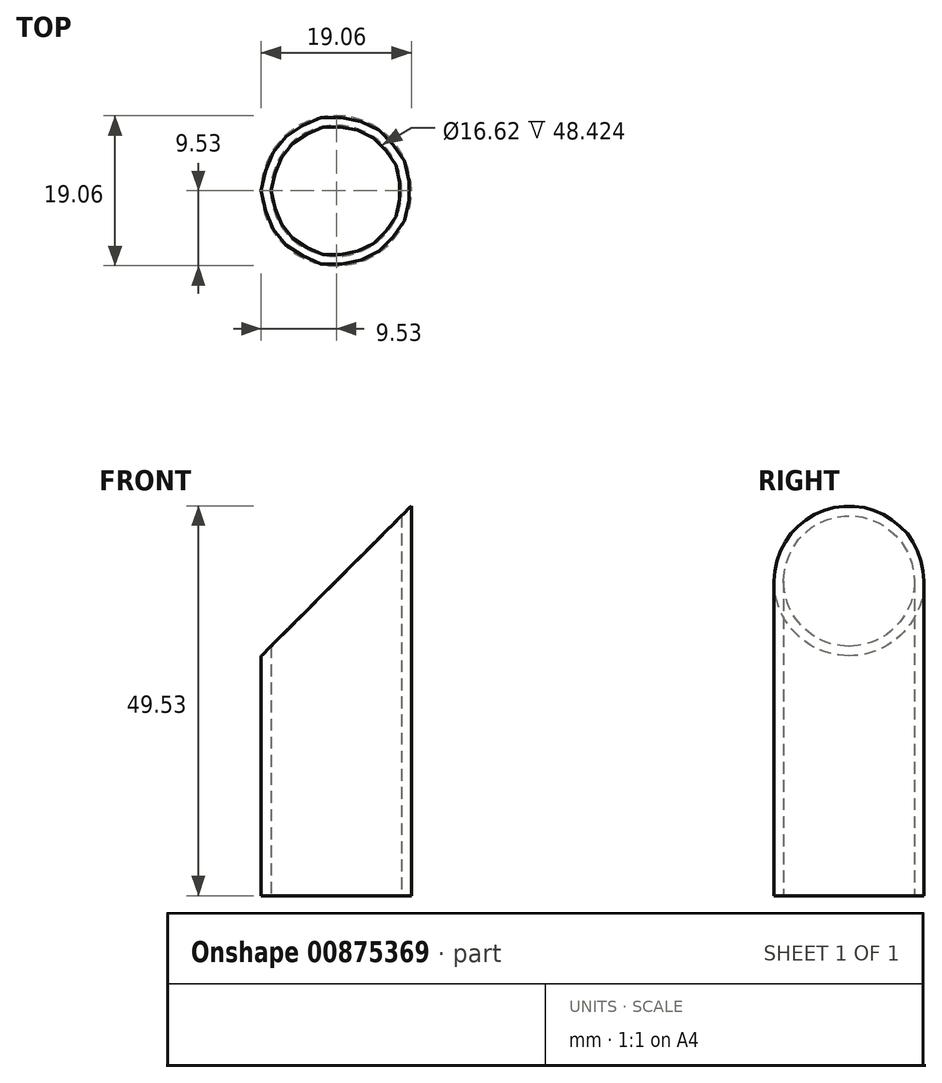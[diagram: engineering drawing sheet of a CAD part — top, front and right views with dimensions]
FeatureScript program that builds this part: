
annotation { "Feature Type Name" : "Feature", "Feature Type Description" : "" }
export const myFeature = defineFeature(function(context is Context, id is Id, definition is map)
    precondition{}
    {
        {
            var Q0;
            Q0=qCreatedBy(makeId("Top.planeOp"),FACE);
            var sketch = newSketch(context, id + "F0", { "sketchPlane" : qUnion([Q0])});
            skCircle(sketch, "E0", {"center": v(0, 0) * mm, "radius": 9.53 * mm});
            skCircle(sketch, "E1.0", {"center": v(0, 0) * mm, "radius": 8.3 * mm});
            skSolve(sketch);
        }
        {
            var Q0;
            Q0=makeQuery(id+"F0.imprint","IMPRINT",FACE,{"disambiguationData":[TD([[makeQuery(id+"F0.imprint","IMPRINT",EDGE,{"derivedFrom":sQuery(id+"F0.wireOp",EDGE,"E0")}),1.0]])]});
            extrude(context, id + "F1", {"entities" : qUnion([Q0]), "depth" : 50 * mm, "offsetDistance" : 25 * mm});
        }
        {
            var Q0;
            Q0=qCreatedBy(makeId("Front.planeOp"),FACE);
            var sketch = newSketch(context, id + "F2", { "sketchPlane" : qUnion([Q0])});
            skLineSegment(sketch, "E2", {"start": v(10, 50) * mm, "end": v(-10, 30) * mm});
            skLineSegment(sketch, "E3", {"start": v(10, 50) * mm, "end": v(-10, 50) * mm});
            skLineSegment(sketch, "E4", {"start": v(-10, 30) * mm, "end": v(-10, 50) * mm});
            skSolve(sketch);
        }
        {
            var Q0;
            Q0=makeQuery(id+"F2.imprint","IMPRINT",FACE,{"disambiguationData":[TD([[makeQuery(id+"F2.imprint","IMPRINT",EDGE,{"derivedFrom":sQuery(id+"F2.wireOp",EDGE,"E2")}),-1.0]])]});
            extrude(context, id + "F3", {"entities" : qUnion([Q0]), "operationType" : NewBodyOperationType.REMOVE, "oppositeDirection" : true, "depth" : 25 * mm, "offsetDistance" : 25 * mm, "symmetric" : true});
        }
    });
